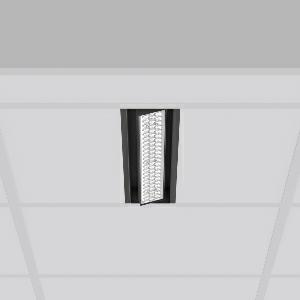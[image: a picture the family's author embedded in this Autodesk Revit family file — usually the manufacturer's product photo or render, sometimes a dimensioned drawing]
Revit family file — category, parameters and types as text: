
# Revit family: tx-move_901728_003_2_76_c452
name_source: partatom
category: Lighting Fixtures
units: mm (PartAtom-declared; Revit-internal decimal feet)

## family parameters
Cut with Voids When Loaded = No
Host = Face
Light Source = No
Part Type = Normal
Room Calculation Point = No
Round Connector Dimension = Use Diameter
Shared = No

## types (1)
- MultiLumen 1 (1 x LED Modul 927, 1950 lm, 2700)
    Apparent Load = 16 VA
    Approval mark = CE
    CIE Flux Codes = 88 96 99 100 100
    Color Rendering = 92
    Color Temperature = 2700
    Default Elevation = 1800 mm
    Description = Series: TX-MOVE
Einlege/Einbau-Flächenstrahler. Housing: sheet steel, powder-coated. Swivel range: 90°. High-efficiency LED units with optimum light control thanks to clear plastic (PC) lens optics. Spezielle Mikrostrukturen reduzieren Gelbsaum. Symmetrical light distribution. Best colour rendering with CRI >90 for fresh products and coloured textiles. Suitable for laying in grid ceiling module 625. Connected converter included in separate gearbox.Suitable for through-wiring.MultiLumen: Luminous flux adjustable in 3 steps. Accessories: Mounting frame for installation in suspended ceilings. Environmentally friendly and resource-saving due to replaceable and recyclable components. 
Colour: deep black, matt (RAL 9005)
Length: 622 mm
Width: 116 mm
Height: 39 mm
Cut-out length: 602 mm
Cut-out width: 98 mm
Recess height: 100 mm
Lamp: LED
Socket: without socket
Colour temperature: 2700K
Colour rendering index (CRI): 90
System power: 16 W
Rated luminous flux: 1950 lm
Luminous efficiency: 122 lm/W
System power 2: 23 W
Rated luminous flux 2: 2750 lm
Luminous efficiency 2: 120 lm/W
System power 3: 31 W
Rated luminous flux 3: 3500 lm
Luminous efficiency 3: 113 lm/W
Control gear: Dimmable EVG, DALI
Protection class: I
Type of protection: IP 20
    Height = 0 mm  [stored 0 ft]
    Lamp = 1 x LED Modul 927
    Lamp Light Flux = 1950 lm
    Lamp count = 1
    Length = 622 mm
    Lifetime = 50000 h
    Luminous efficacy = 122 lm/W
    Manufacturer = RZB
    ModVariant = No
    Model = 901728.003.2.76
    Mounting Place = Ceiling, Wall
    Mounting Type = Recessed
    Number of Poles = 1
    OnlyDefault = Yes
    Power Factor = 1
    Product Name = TX-MOVE
    Product group = Recessed projectors
    ProductGroupID = 401
    Protection Class = Protection class I
    Protection Degree = IP 20
    RLX_Detail_Level = 1
    RLX_Emergency_Light_Flux = 0 lm
    RLX_Emergency_Type = 0
    RLX_Emergency_Type_DB = No
    RlxData = <blob elided: 28205 chars, md5=5ac4c599>
    Socket = socket
    Standby Power = 0 W
    System Light Flux = 1950 lm
    System Power = 16 W
    Type Comments = MultiLumen 1
    Type Image = 901729.003.jpg
    URL = http://relux.com
    VarID = multilumen_1
    Voltage = 230 V
    Voltage Range = 220-240 V
    Weight = 0.00 kg
    Width = 116 mm

note: [stored X ft] marks values corroborated as IEEE doubles in the binary element streams (Revit-internal decimal feet)

## geometry (parser evidence)
native form markers: Blend x4, Sweep x15
no freeform markers — native parametric forms only
